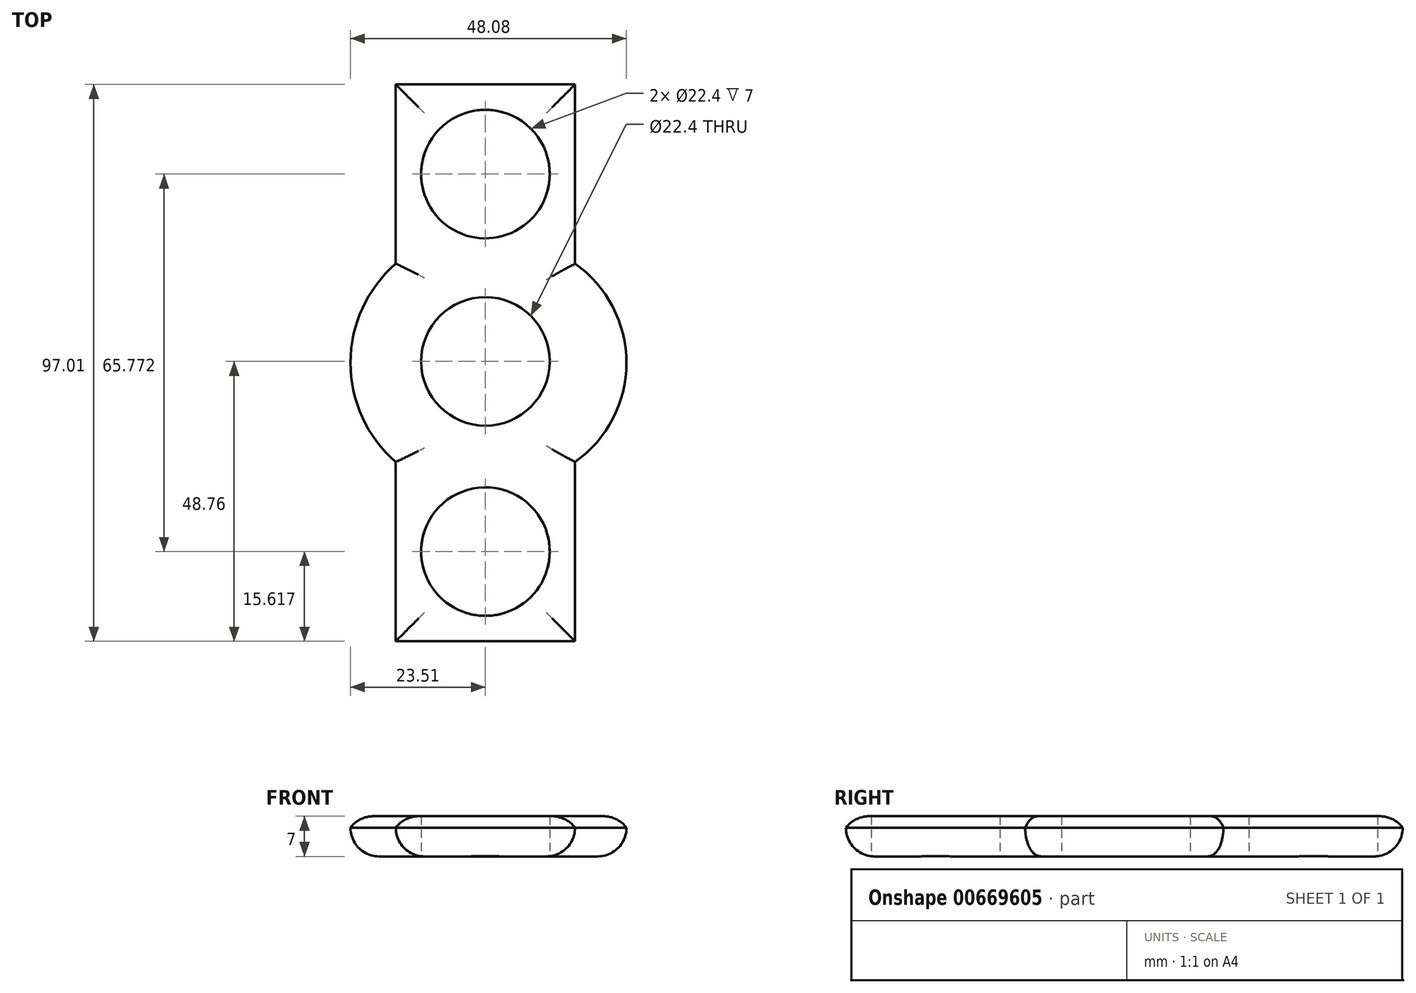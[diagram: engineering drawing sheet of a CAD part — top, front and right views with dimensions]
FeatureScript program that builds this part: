
annotation { "Feature Type Name" : "Feature", "Feature Type Description" : "" }
export const myFeature = defineFeature(function(context is Context, id is Id, definition is map)
    precondition{}
    {
        {
            var Q0;
            Q0=qCreatedBy(makeId("Top.planeOp"),FACE);
            var sketch = newSketch(context, id + "F0", { "sketchPlane" : qUnion([Q0])});
            skCircle(sketch, "E0", {"center": v(0, 0) * mm, "radius": 11.2 * mm});
            skCircle(sketch, "E1", {"center": v(0, 0) * mm, "radius": 13.2 * mm});
            skCircle(sketch, "E2", {"center": v(0, 32.63) * mm, "radius": 11.2 * mm});
            skCircle(sketch, "E3.cCircle", {"center": v(0, 32.63) * mm, "radius": 15.62 * mm, "construction": true});
            skLineSegment(sketch, "E3.0", {"start": v(-15.62, 48.25) * mm, "end": v(15.62, 48.25) * mm});
            skLineSegment(sketch, "E3.1", {"start": v(15.62, 48.25) * mm, "end": v(15.62, 17.01) * mm});
            skLineSegment(sketch, "E3.2", {"start": v(15.62, 17.01) * mm, "end": v(-15.62, 17.01) * mm});
            skLineSegment(sketch, "E3.3", {"start": v(-15.62, 17.01) * mm, "end": v(-15.62, 48.25) * mm});
            skPoint(sketch, "E3.0.midPoint", {"position": v(0, 48.25) * mm});
            skCircle(sketch, "E4.1.0", {"center": v(0, -33.14) * mm, "radius": 15.62 * mm, "construction": true});
            skCircle(sketch, "E4.1.1", {"center": v(0, -33.14) * mm, "radius": 11.2 * mm});
            skLineSegment(sketch, "E4.1.2", {"start": v(-15.62, -48.76) * mm, "end": v(-15.62, -17.52) * mm});
            skLineSegment(sketch, "E4.1.3", {"start": v(-15.62, -17.52) * mm, "end": v(15.62, -17.52) * mm});
            skLineSegment(sketch, "E4.1.4", {"start": v(15.62, -17.52) * mm, "end": v(15.62, -48.76) * mm});
            skLineSegment(sketch, "E4.1.5", {"start": v(15.62, -48.76) * mm, "end": v(-15.62, -48.76) * mm});
            skPoint(sketch, "E4.center", {"position": v(0, -0.26) * mm});
            skArc(sketch, "E5", {"start": v(-15.62, 17.01) * mm, "mid": v(-23.51, -0.26) * mm, "end": v(-15.62, -17.52) * mm});
            skArc(sketch, "E6", {"start": v(15.62, -17.52) * mm, "mid": v(24.57, -0.26) * mm, "end": v(15.62, 17.01) * mm});
            skSolve(sketch);
        }
        {
            var Q0;
            Q0=makeQuery(id+"F0.imprint","IMPRINT",FACE,{"disambiguationData":[TD([[makeQuery(id+"F0.imprint","IMPRINT",EDGE,{"derivedFrom":sQuery(id+"F0.wireOp",EDGE,"E1")}),-1.0]])]});
            var Q1;
            Q1=makeQuery(id+"F0.imprint","IMPRINT",FACE,{"disambiguationData":[TD([[makeQuery(id+"F0.imprint","IMPRINT",EDGE,{"derivedFrom":sQuery(id+"F0.wireOp",EDGE,"E0")}),-1.0]])]});
            var Q2;
            Q2=makeQuery(id+"F0.imprint","IMPRINT",FACE,{"disambiguationData":[TD([[makeQuery(id+"F0.imprint","IMPRINT",EDGE,{"derivedFrom":sQuery(id+"F0.wireOp",EDGE,"E2")}),-1.0]])]});
            var Q3;
            Q3=makeQuery(id+"F0.imprint","IMPRINT",FACE,{"disambiguationData":[TD([[makeQuery(id+"F0.imprint","IMPRINT",EDGE,{"derivedFrom":sQuery(id+"F0.wireOp",EDGE,"E4.1.1")}),-1.0]])]});
            extrude(context, id + "F1", {"entities" : qUnion([Q0, Q1, Q2, Q3]), "depth" : 7 * mm, "offsetDistance" : 25 * mm});
        }
        {
            var Q0;
            Q0=makeQuery(id+"F1.opExtrude","CAP_EDGE",EDGE,{"disambiguationData":[OSD([sQuery(id+"F0.wireOp",EDGE,"E5")])],"isStart":true});
            var Q1;
            Q1=makeQuery(id+"F1.opExtrude","CAP_EDGE",EDGE,{"disambiguationData":[OSD([sQuery(id+"F0.wireOp",EDGE,"E3.3")])],"isStart":true});
            var Q2;
            Q2=makeQuery(id+"F1.opExtrude","CAP_EDGE",EDGE,{"disambiguationData":[OSD([sQuery(id+"F0.wireOp",EDGE,"E3.0")])],"isStart":true});
            var Q3;
            Q3=makeQuery(id+"F1.opExtrude","CAP_EDGE",EDGE,{"disambiguationData":[OSD([sQuery(id+"F0.wireOp",EDGE,"E3.1")])],"isStart":true});
            var Q4;
            Q4=makeQuery(id+"F1.opExtrude","CAP_EDGE",EDGE,{"disambiguationData":[OSD([sQuery(id+"F0.wireOp",EDGE,"E6")])],"isStart":true});
            var Q5;
            Q5=makeQuery(id+"F1.opExtrude","CAP_EDGE",EDGE,{"disambiguationData":[OSD([sQuery(id+"F0.wireOp",EDGE,"E4.1.4")])],"isStart":true});
            var Q6;
            Q6=makeQuery(id+"F1.opExtrude","CAP_EDGE",EDGE,{"disambiguationData":[OSD([sQuery(id+"F0.wireOp",EDGE,"E4.1.5")])],"isStart":true});
            var Q7;
            Q7=makeQuery(id+"F1.opExtrude","CAP_EDGE",EDGE,{"disambiguationData":[OSD([sQuery(id+"F0.wireOp",EDGE,"E4.1.2")])],"isStart":true});
            fillet(context, id + "F2", {"entities" : qUnion([Q0, Q1, Q2, Q3, Q4, Q5, Q6, Q7]), "radius" : 5 * mm, "tangentPropagation" : true, "allowEdgeOverflow" : false});
        }
        {
            var Q0;
            Q0=makeQuery(id+"F1.opExtrude","CAP_EDGE",EDGE,{"disambiguationData":[OSD([sQuery(id+"F0.wireOp",EDGE,"E3.0")])],"isStart":false});
            var Q1;
            Q1=makeQuery(id+"F1.opExtrude","CAP_EDGE",EDGE,{"disambiguationData":[OSD([sQuery(id+"F0.wireOp",EDGE,"E3.1")])],"isStart":false});
            var Q2;
            Q2=makeQuery(id+"F1.opExtrude","CAP_EDGE",EDGE,{"disambiguationData":[OSD([sQuery(id+"F0.wireOp",EDGE,"E6")])],"isStart":false});
            var Q3;
            Q3=makeQuery(id+"F1.opExtrude","CAP_EDGE",EDGE,{"disambiguationData":[OSD([sQuery(id+"F0.wireOp",EDGE,"E4.1.4")])],"isStart":false});
            var Q4;
            Q4=makeQuery(id+"F1.opExtrude","CAP_EDGE",EDGE,{"disambiguationData":[OSD([sQuery(id+"F0.wireOp",EDGE,"E4.1.5")])],"isStart":false});
            var Q5;
            Q5=makeQuery(id+"F1.opExtrude","CAP_EDGE",EDGE,{"disambiguationData":[OSD([sQuery(id+"F0.wireOp",EDGE,"E4.1.2")])],"isStart":false});
            var Q6;
            Q6=makeQuery(id+"F1.opExtrude","CAP_EDGE",EDGE,{"disambiguationData":[OSD([sQuery(id+"F0.wireOp",EDGE,"E5")])],"isStart":false});
            var Q7;
            Q7=makeQuery(id+"F1.opExtrude","CAP_EDGE",EDGE,{"disambiguationData":[OSD([sQuery(id+"F0.wireOp",EDGE,"E3.3")])],"isStart":false});
            fillet(context, id + "F3", {"entities" : qUnion([Q0, Q1, Q2, Q3, Q4, Q5, Q6, Q7]), "radius" : 5 * mm, "tangentPropagation" : true, "allowEdgeOverflow" : false});
        }
    });
